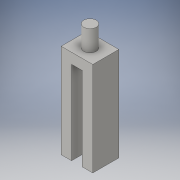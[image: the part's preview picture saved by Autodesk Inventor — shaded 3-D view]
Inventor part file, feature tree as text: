
AUTODESK INVENTOR PART (.ipt)
format: ipt  version: 2016 (Build 200138000, 138)  size: 114,176 bytes
history: native  units: in
note: dims shown in document units (in); Inventor stores cm internally (conversion verified against a paired STEP export)
features: extrude x3, sketch x3
ambient origin geometry x8: Origin, YZ Plane, XZ Plane, XY Plane, X Axis, Y Axis, Z Axis, Center Point
bodies: Solid1 (feature_tree)
feature tree (6):
  extrude  "Extrusion1"  Depth=0.25in
  extrude  "Extrusion2"  Depth=0.1in
  extrude  "Extrusion3"  Depth=0.1in
  sketch  "Sketch1"  dims[d0=0.303in d1=0.25in]
  sketch  "Sketch2"  dims[d2=0.1in d3=0.0in d4=0.1181in]
  sketch  "Sketch3"  dims[d5=0.2in d6=0.0in d7=0.1in d8=0.1in d9=0.103in d10=0.8in d11=0.0in]
